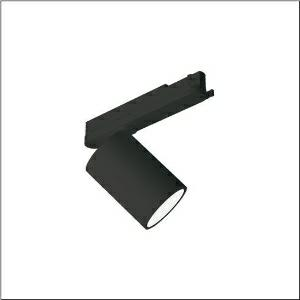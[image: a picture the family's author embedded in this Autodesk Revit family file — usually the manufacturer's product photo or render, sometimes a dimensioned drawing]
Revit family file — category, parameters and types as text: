
# Revit family: spot_31_51sf34mad4b
name_source: partatom
category: Lighting Fixtures
units: mm (PartAtom-declared; Revit-internal decimal feet)

## family parameters
Cut with Voids When Loaded = No
Host = Face
Light Source = No
Part Type = Normal
Room Calculation Point = No
Round Connector Dimension = Use Diameter
Shared = No

## types (1)
- --- (1 x LED, 5250 lm, 41.4 W, 4000K)
    Apparent Load = 41 VA
    CIE Flux Codes = 93 97 100 100 100
    Color Rendering = 90
    Color Temperature = 4000K
    Default Elevation = 1800 mm
    Description = Spot 31, directional spotlight, light control with lens, of PMMA, LED rated luminous flux: 5.040lm, light colour: 940, with 3-phase adapter, mains connection: 220..240V, AC, 50/60Hz, of aluminium, jet black (RAL 9005), length: 213mm, diameter: 90mm, protection rating (complete): IP20, insulation class (complete): insulation class I (protective earthing), certification: CE, impact resistance: IK02, permissible ambient temperature for indoor applications: -20..+40°C, packaging unit: 1 piece
    Height = 175 mm
    Lamp = 1 x LED
    Lamp Light Flux = 5250 lm
    Lamp Power = 41.4 W
    Lamp count = 1
    Length = 90 mm
    Luminous efficacy = 127 lm/W
    Manufacturer = Siteco
    ModVariant = No
    Model = 51SF34MAD4B
    Mounting Place = Ceiling
    Mounting Type = Pendant
    Number of Poles = 1
    OnlyDefault = Yes
    Power Factor = 1
    Product Name = Spot 31
    Product group = directional spotlight
    ProductGroupID = 906
    Protection Class = Protection class I
    Protection Degree = IP 20
    RLX_Detail_Level = 1
    RLX_Emergency_Light_Flux = 0 lm
    RLX_Emergency_Type = 0
    RLX_Emergency_Type_DB = No
    RlxData = <blob elided: 20901 chars, md5=aa311c2b>
    Socket = socket
    Standby Power = 0 W
    System Light Flux = 5250 lm
    System Power = 41 W
    Type Comments = factory setting: luminous flux: 100 % | (ON | ON | ON | ON) | 1050 mA
    Type Image = l_1273723.jpg
    URL = http://relux.com
    VarID = @adj_146250
    Voltage = 0 V
    Weight = 0.00 kg
    Width = 0 mm  [stored 0 ft]

note: [stored X ft] marks values corroborated as IEEE doubles in the binary element streams (Revit-internal decimal feet)

## geometry (parser evidence)
native form markers: Blend x4, Sweep x13
no freeform markers — native parametric forms only
